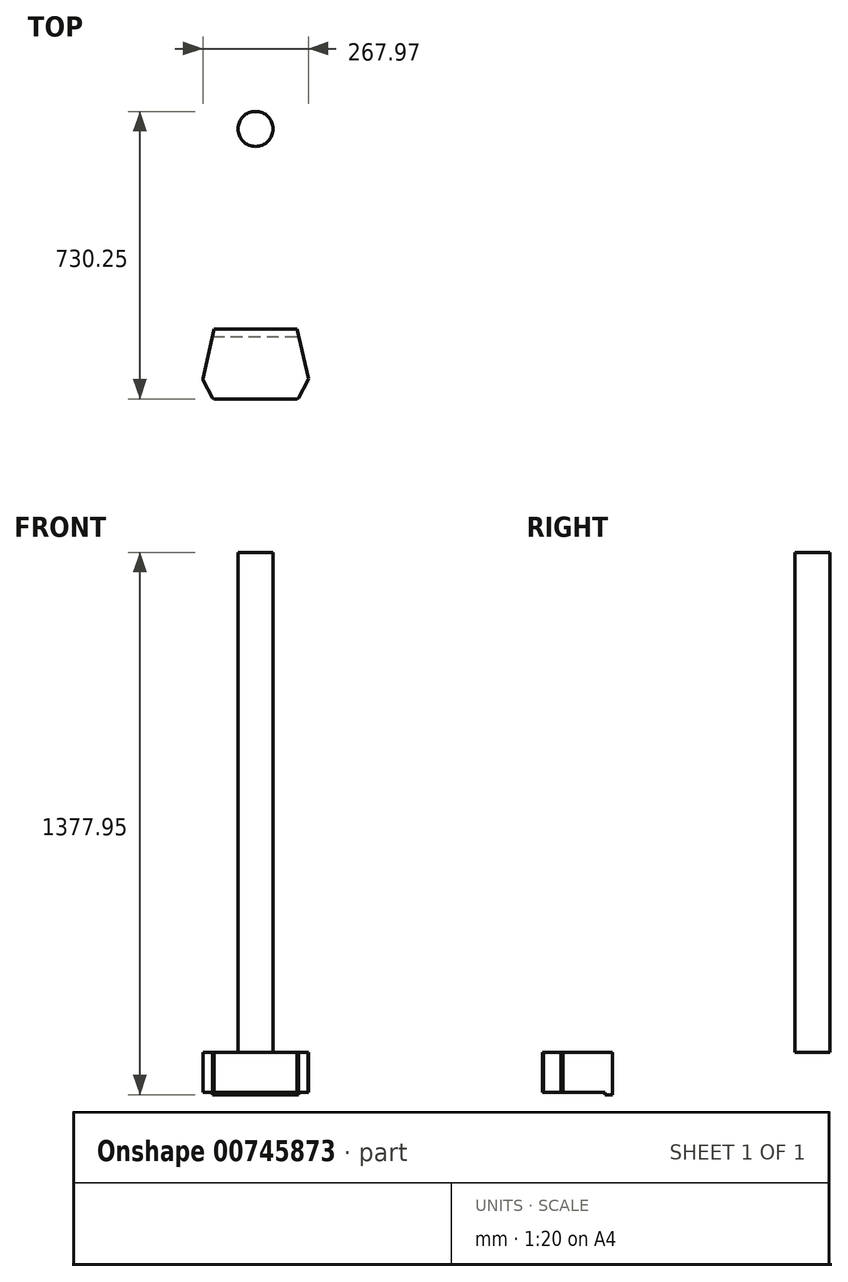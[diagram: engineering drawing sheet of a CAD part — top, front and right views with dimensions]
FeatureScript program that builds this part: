
annotation { "Feature Type Name" : "Feature", "Feature Type Description" : "" }
export const myFeature = defineFeature(function(context is Context, id is Id, definition is map)
    precondition{}
    {
        {
            var Q0;
            Q0=qCreatedBy(makeId("Top.planeOp"),FACE);
            var sketch = newSketch(context, id + "F0", { "sketchPlane" : qUnion([Q0])});
            skLineSegment(sketch, "E0", {"start": v(-153.63, -90.08) * mm, "end": v(138.47, -90.08) * mm});
            skLineSegment(sketch, "E1", {"start": v(138.47, -90.08) * mm, "end": v(97.2, 87.72) * mm});
            skLineSegment(sketch, "E2", {"start": v(97.2, 87.72) * mm, "end": v(-112.35, 87.72) * mm});
            skLineSegment(sketch, "E3", {"start": v(-112.35, 87.72) * mm, "end": v(-153.63, -90.08) * mm});
            skSolve(sketch);
        }
        {
            var Q0;
            Q0=makeQuery(id+"F0.imprint","IMPRINT",FACE,{"disambiguationData":[TD([[makeQuery(id+"F0.imprint","IMPRINT",EDGE,{"derivedFrom":sQuery(id+"F0.wireOp",EDGE,"E0")}),1.0]])]});
            extrude(context, id + "F1", {"entities" : qUnion([Q0]), "depth" : 107.95 * mm, "offsetDistance" : 25.4 * mm});
        }
        {
            var Q0;
            Q0=makeQuery(id+"F1.opExtrude","CAP_FACE",FACE,{"disambiguationData":[OSD([sQuery(id+"F0.wireOp",EDGE,"E0"),sQuery(id+"F0.wireOp",EDGE,"E1"),sQuery(id+"F0.wireOp",EDGE,"E2"),sQuery(id+"F0.wireOp",EDGE,"E3")])],"isStart":true});
            var sketch = newSketch(context, id + "F2", { "sketchPlane" : qUnion([Q0])});
            skLineSegment(sketch, "E4", {"start": v(-153.63, 90.08) * mm, "end": v(138.47, 90.08) * mm});
            skLineSegment(sketch, "E5", {"start": v(-116.77, -68.67) * mm, "end": v(101.62, -68.67) * mm});
            skLineSegment(sketch, "E6", {"start": v(138.47, 90.08) * mm, "end": v(101.62, -68.67) * mm});
            skLineSegment(sketch, "E7", {"start": v(-153.63, 90.08) * mm, "end": v(-116.77, -68.67) * mm});
            skSolve(sketch);
        }
        {
            var Q0;
            Q0=qSketchRegion(id+"F2",true);
            extrude(context, id + "F3", {"entities" : qUnion([Q0]), "operationType" : NewBodyOperationType.REMOVE, "oppositeDirection" : true, "depth" : 6.35 * mm, "offsetDistance" : 25.4 * mm});
        }
        {
            var Q0;
            Q0=makeQuery(id+"F1.opExtrude","SWEPT_EDGE",EDGE,{"disambiguationData":[OSD([sQuery(id+"F0.wireOp",EDGE,"E0"),sQuery(id+"F0.wireOp",EDGE,"E1")])]});
            var Q1;
            Q1=makeQuery(id+"F1.opExtrude","SWEPT_EDGE",EDGE,{"disambiguationData":[OSD([sQuery(id+"F0.wireOp",EDGE,"E0"),sQuery(id+"F0.wireOp",EDGE,"E3")])]});
            chamfer(context, id + "F4", {"entities" : qUnion([Q0, Q1]), "chamferType" : ChamferType.TWO_OFFSETS, "width1" : 38.1 * mm, "oppositeDirection" : false, "width2" : 50.8 * mm, "tangentPropagation" : true});
        }
        {
            var Q0;
            {var subQ0=sQuery(id+"F0.wireOp",EDGE,"E0");Q0=makeQuery(id+"F4.opChamfer","BLEND_EDGE",EDGE,{"blendedFrom":[makeQuery(id+"F1.opExtrude","SWEPT_EDGE",EDGE,{"disambiguationData":[OSD([subQ0,sQuery(id+"F0.wireOp",EDGE,"E1")])]}),makeQuery(id+"F1.opExtrude","SWEPT_FACE",FACE,{"disambiguationData":[OSD([subQ0])]})],"blendedInto":[makeQuery(id+"F1.opExtrude","SWEPT_FACE",FACE,{"disambiguationData":[OSD([subQ0])]})]});}
            var Q1;
            {var subQ0=sQuery(id+"F0.wireOp",EDGE,"E1");Q1=makeQuery(id+"F4.opChamfer","BLEND_EDGE",EDGE,{"blendedFrom":[makeQuery(id+"F1.opExtrude","SWEPT_EDGE",EDGE,{"disambiguationData":[OSD([sQuery(id+"F0.wireOp",EDGE,"E0"),subQ0])]}),makeQuery(id+"F1.opExtrude","SWEPT_FACE",FACE,{"disambiguationData":[OSD([subQ0])]})],"blendedInto":[makeQuery(id+"F1.opExtrude","SWEPT_FACE",FACE,{"disambiguationData":[OSD([subQ0])]})]});}
            var Q2;
            {var subQ0=sQuery(id+"F0.wireOp",EDGE,"E0");Q2=makeQuery(id+"F4.opChamfer","BLEND_EDGE",EDGE,{"blendedFrom":[makeQuery(id+"F1.opExtrude","SWEPT_EDGE",EDGE,{"disambiguationData":[OSD([subQ0,sQuery(id+"F0.wireOp",EDGE,"E3")])]}),makeQuery(id+"F1.opExtrude","SWEPT_FACE",FACE,{"disambiguationData":[OSD([subQ0])]})],"blendedInto":[makeQuery(id+"F1.opExtrude","SWEPT_FACE",FACE,{"disambiguationData":[OSD([subQ0])]})]});}
            var Q3;
            {var subQ0=sQuery(id+"F0.wireOp",EDGE,"E3");Q3=makeQuery(id+"F4.opChamfer","BLEND_EDGE",EDGE,{"blendedFrom":[makeQuery(id+"F1.opExtrude","SWEPT_EDGE",EDGE,{"disambiguationData":[OSD([sQuery(id+"F0.wireOp",EDGE,"E0"),subQ0])]}),makeQuery(id+"F1.opExtrude","SWEPT_FACE",FACE,{"disambiguationData":[OSD([subQ0])]})],"blendedInto":[makeQuery(id+"F1.opExtrude","SWEPT_FACE",FACE,{"disambiguationData":[OSD([subQ0])]})]});}
            chamfer(context, id + "F5", {"entities" : qUnion([Q0, Q1, Q2, Q3]), "width" : 2.54 * mm, "tangentPropagation" : true});
        }
        {
            var Q0;
            Q0=makeQuery(id+"F1.opExtrude","CAP_FACE",FACE,{"disambiguationData":[OSD([sQuery(id+"F0.wireOp",EDGE,"E0"),sQuery(id+"F0.wireOp",EDGE,"E1"),sQuery(id+"F0.wireOp",EDGE,"E2"),sQuery(id+"F0.wireOp",EDGE,"E3")])],"isStart":false});
            var sketch = newSketch(context, id + "F6", { "sketchPlane" : qUnion([Q0])});
            skLineSegment(sketch, "E8.bottom", {"start": v(-693.38, 1281.52) * mm, "end": v(678.22, 1281.52) * mm, "construction": true});
            skLineSegment(sketch, "E8.top", {"start": v(-693.38, -90.08) * mm, "end": v(678.22, -90.08) * mm, "construction": true});
            skLineSegment(sketch, "E8.left", {"start": v(-693.38, 1281.52) * mm, "end": v(-693.38, -90.08) * mm, "construction": true});
            skLineSegment(sketch, "E8.right", {"start": v(678.22, 1281.52) * mm, "end": v(678.22, -90.08) * mm, "construction": true});
            skLineSegment(sketch, "E9", {"start": v(678.22, 1281.52) * mm, "end": v(-693.38, -90.08) * mm, "construction": true});
            skLineSegment(sketch, "E10", {"start": v(-693.38, 1281.52) * mm, "end": v(678.22, -90.08) * mm, "construction": true});
            skCircle(sketch, "E11", {"center": v(-7.58, 595.72) * mm, "radius": 44.45 * mm});
            skSolve(sketch);
        }
        {
            var Q0;
            Q0=qSketchRegion(id+"F6",true);
            extrude(context, id + "F7", {"entities" : qUnion([Q0]), "depth" : 1270 * mm, "offsetDistance" : 25.4 * mm});
        }
        {
            var Q0;
            Q0=qSketchRegion(id+"F6",true);
            extrude(context, id + "F8", {"entities" : qUnion([Q0]), "operationType" : NewBodyOperationType.ADD, "depth" : 25.4 * mm, "offsetDistance" : 25.4 * mm});
        }
        {
            var Q0;
            Q0 = qSketchRegion(id + "F6", true);
            extrude(context, id + "F9", {"entities" : qUnion([Q0]), "operationType" : NewBodyOperationType.ADD, "depth" : 25.4 * mm, "offsetDistance" : 25.4 * mm});
        }
    });
